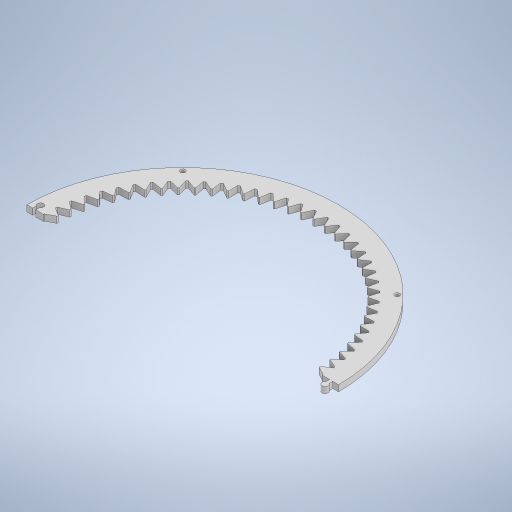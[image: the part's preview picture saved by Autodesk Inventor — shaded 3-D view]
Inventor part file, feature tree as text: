
AUTODESK INVENTOR PART (.ipt)
format: ipt  version: 2023 (Build 270158000, 158)  size: 519,680 bytes
history: native  units: in
note: dims shown in document units (in); Inventor stores cm internally (conversion verified against a paired STEP export)
features: sketch x2, extrude x1, hole x1
ambient origin geometry x8: Origin, YZ Plane, XZ Plane, XY Plane, X Axis, Y Axis, Z Axis, Center Point
bodies: Body1 (feature_tree)
feature tree (4):
  sketch  "Sketch1"  dims[d0=9.8425in d1=8.7992in]
  extrude  "Extrusion2"  Depth=8.7992in
  hole  "Hole1"  [1 undecoded]
  sketch  "Sketch2"  dims[d2=0.2953in d3=30.0deg d4=120.0deg d7=0.0394in d8=0.0394in d9=0.7874in d11=360.0deg d13=27.5591in d15=360.0deg d17=0.1969in d18=0.0in d19=9.311in d20=45.0deg d21=1.5748in d23=360.0deg d25=0.0945in d26=0.2362in d27=0.1575in d28=0.0787in d29=90.0deg d30=0.315in d31=0.8108in d32=9.8425in d33=8.7992in d34=9.2717in]
note: 1 required parameter value undecoded (feature->parameter linkage not recoverable at this tier; creation-order binding heuristic only, values carry confidence <= 0.55)
